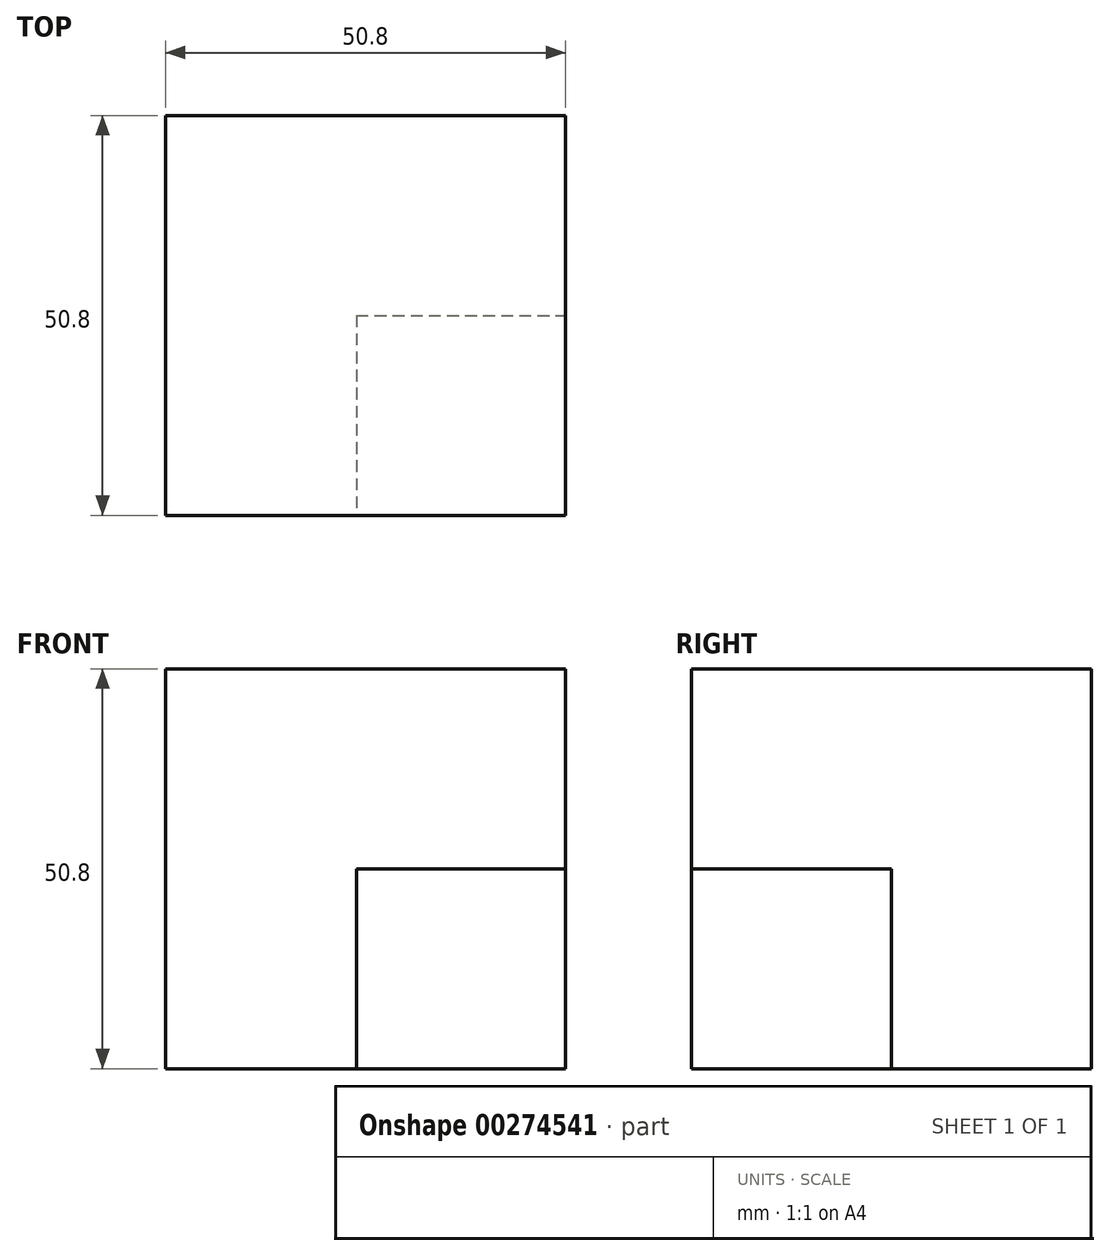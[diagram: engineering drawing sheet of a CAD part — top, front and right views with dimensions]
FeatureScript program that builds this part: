
annotation { "Feature Type Name" : "Feature", "Feature Type Description" : "" }
export const myFeature = defineFeature(function(context is Context, id is Id, definition is map)
    precondition{}
    {
        {
            var Q0;
            Q0=qCreatedBy(makeId("Front.planeOp"),FACE);
            var sketch = newSketch(context, id + "F0", { "sketchPlane" : qUnion([Q0])});
            skLineSegment(sketch, "E0.bottom", {"start": v(-44.87, 50.8) * mm, "end": v(5.93, 50.8) * mm});
            skLineSegment(sketch, "E0.top", {"start": v(-44.87, 0) * mm, "end": v(5.93, 0) * mm});
            skLineSegment(sketch, "E0.left", {"start": v(-44.87, 50.8) * mm, "end": v(-44.87, 0) * mm});
            skLineSegment(sketch, "E0.right", {"start": v(5.93, 50.8) * mm, "end": v(5.93, 0) * mm});
            skSolve(sketch);
        }
        {
            var Q0;
            Q0=makeQuery(id+"F0.imprint","IMPRINT",FACE,{"disambiguationData":[TD([[makeQuery(id+"F0.imprint","IMPRINT",EDGE,{"derivedFrom":sQuery(id+"F0.wireOp",EDGE,"E0.bottom")}),-1.0]])]});
            extrude(context, id + "F1", {"entities" : qUnion([Q0]), "depth" : 50.8 * mm});
        }
        {
            var Q0;
            Q0=qCreatedBy(makeId("Top.planeOp"),FACE);
            var sketch = newSketch(context, id + "F2", { "sketchPlane" : qUnion([Q0])});
            skLineSegment(sketch, "E1.bottom", {"start": v(-45.45, 0) * mm, "end": v(-20.05, 0) * mm});
            skLineSegment(sketch, "E1.top", {"start": v(-45.45, -50.8) * mm, "end": v(-20.05, -50.8) * mm});
            skLineSegment(sketch, "E1.left", {"start": v(-45.45, 0) * mm, "end": v(-45.45, -50.8) * mm});
            skLineSegment(sketch, "E1.right", {"start": v(-20.05, 0) * mm, "end": v(-20.05, -50.8) * mm});
            skLineSegment(sketch, "E2.bottom", {"start": v(-45.45, -25.4) * mm, "end": v(5.35, -25.4) * mm});
            skLineSegment(sketch, "E2.top", {"start": v(-45.45, -50.8) * mm, "end": v(5.35, -50.8) * mm});
            skLineSegment(sketch, "E2.left", {"start": v(-45.45, -25.4) * mm, "end": v(-45.45, -50.8) * mm});
            skLineSegment(sketch, "E2.right", {"start": v(5.35, -25.4) * mm, "end": v(5.35, -50.8) * mm});
            skSolve(sketch);
        }
        {
            var Q0;
            Q0 = qSketchRegion(id + "F2", true);
            extrude(context, id + "F3", {"entities" : qUnion([Q0]), "operationType" : NewBodyOperationType.REMOVE, "oppositeDirection" : true, "depth" : 50.8 * mm});
        }
        {
            var Q0;
            Q0=qCreatedBy(makeId("Top.planeOp"),FACE);
            var sketch = newSketch(context, id + "F4", { "sketchPlane" : qUnion([Q0])});
            skLineSegment(sketch, "E3.bottom", {"start": v(-25.4, -29.79) * mm, "end": v(0, -29.79) * mm});
            skLineSegment(sketch, "E3.top", {"start": v(-25.4, -4.39) * mm, "end": v(0, -4.39) * mm});
            skLineSegment(sketch, "E3.left", {"start": v(-25.4, -29.79) * mm, "end": v(-25.4, -4.39) * mm});
            skLineSegment(sketch, "E3.right", {"start": v(0, -29.79) * mm, "end": v(0, -4.39) * mm});
            skSolve(sketch);
        }
        {
            var Q0;
            Q0 = qSketchRegion(id + "F4", true);
            extrude(context, id + "F5", {"entities" : qUnion([Q0]), "operationType" : NewBodyOperationType.REMOVE, "oppositeDirection" : true, "depth" : 101.6 * mm});
        }
        {
            var Q0;
            Q0=makeQuery(id+"F1.opExtrude","CAP_FACE",FACE,{"disambiguationData":[OSD([sQuery(id+"F0.wireOp",EDGE,"E0.bottom"),sQuery(id+"F0.wireOp",EDGE,"E0.top"),sQuery(id+"F0.wireOp",EDGE,"E0.left"),sQuery(id+"F0.wireOp",EDGE,"E0.right")])],"isStart":false});
            var sketch = newSketch(context, id + "F6", { "sketchPlane" : qUnion([Q0])});
            skLineSegment(sketch, "E4.bottom", {"start": v(5.93, 0) * mm, "end": v(-20.62, 0) * mm});
            skLineSegment(sketch, "E4.top", {"start": v(5.93, 25.4) * mm, "end": v(-20.62, 25.4) * mm});
            skLineSegment(sketch, "E4.left", {"start": v(5.93, 0) * mm, "end": v(5.93, 25.4) * mm});
            skLineSegment(sketch, "E4.right", {"start": v(-20.62, 0) * mm, "end": v(-20.62, 25.4) * mm});
            skSolve(sketch);
        }
        {
            var Q0;
            Q0=makeQuery(id+"F6.imprint","IMPRINT",FACE,{"disambiguationData":[TD([[makeQuery(id+"F6.imprint","IMPRINT",EDGE,{"derivedFrom":sQuery(id+"F6.wireOp",EDGE,"E4.bottom")}),1.0]])]});
            extrude(context, id + "F7", {"entities" : qUnion([Q0]), "operationType" : NewBodyOperationType.REMOVE, "oppositeDirection" : true, "depth" : 25.4 * mm});
        }
    });
